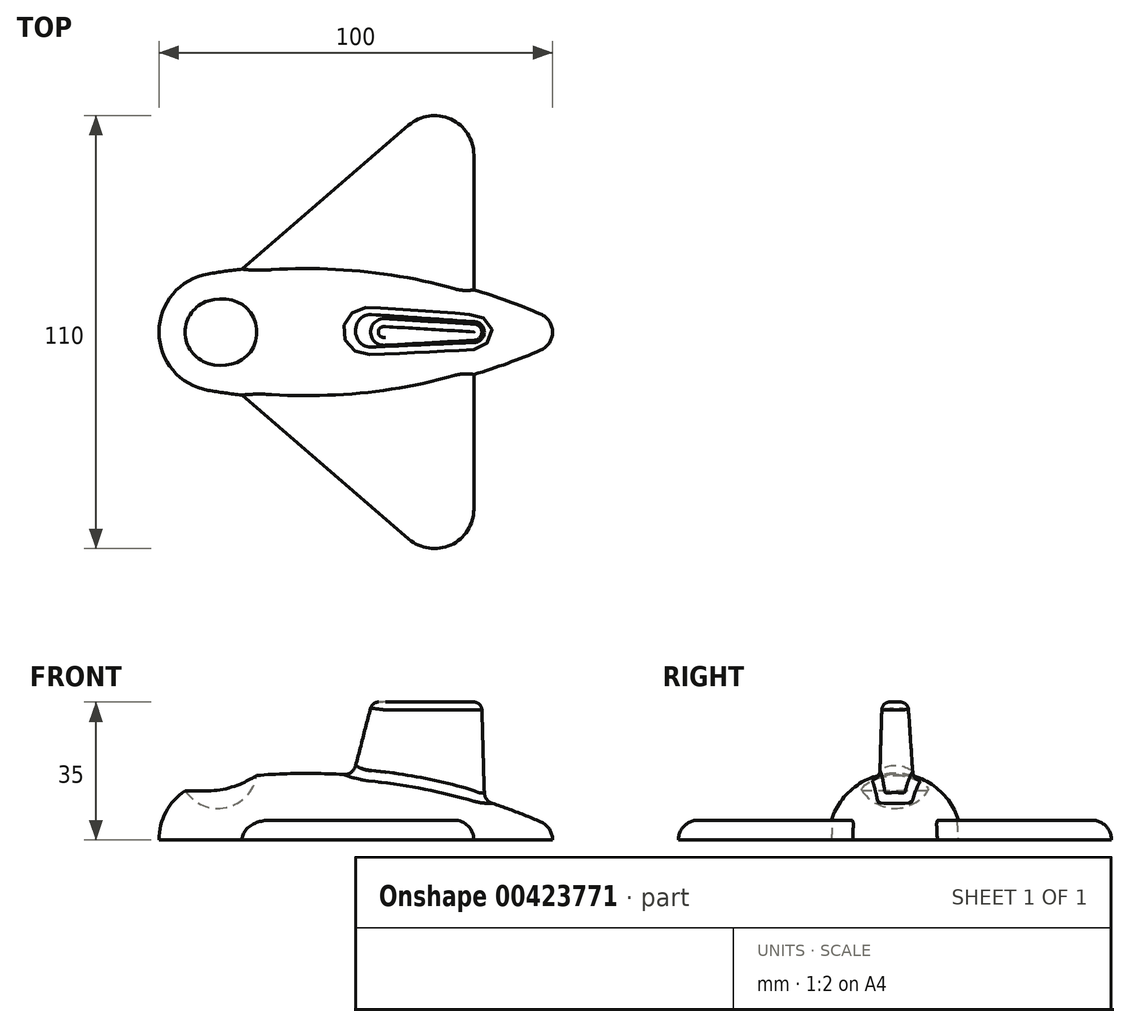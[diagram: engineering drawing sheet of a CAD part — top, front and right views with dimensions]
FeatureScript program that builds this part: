
annotation { "Feature Type Name" : "Feature", "Feature Type Description" : "" }
export const myFeature = defineFeature(function(context is Context, id is Id, definition is map)
    precondition{}
    {
        {
            var Q0;
            Q0=qCreatedBy(makeId("Top.planeOp"),FACE);
            var sketch = newSketch(context, id + "F0", { "sketchPlane" : qUnion([Q0])});
            skArc(sketch, "E0", {"start": v(-60.05, 14.8) * mm, "mid": v(-69, 9.68) * mm, "end": v(-72.55, 0) * mm});
            skArc(sketch, "E1", {"start": v(27.45, 0) * mm, "mid": v(26.63, 2.75) * mm, "end": v(24.44, 4.6) * mm});
            skArc(sketch, "E2", {"start": v(24.44, 4.6) * mm, "mid": v(-17.07, 15.8) * mm, "end": v(-60.05, 14.8) * mm});
            skLineSegment(sketch, "E3", {"start": v(-72.55, 0) * mm, "end": v(27.45, 0) * mm});
            skPoint(sketch, "E4.orphan", {"position": v(-79.31, 0) * mm});
            skSolve(sketch);
        }
        {
            var Q0;
            Q0=makeQuery(id+"F0.imprint","IMPRINT",FACE,{"disambiguationData":[TD([[makeQuery(id+"F0.imprint","IMPRINT",EDGE,{"derivedFrom":sQuery(id+"F0.wireOp",EDGE,"E0")}),1.0]])]});
            var Q1;
            Q1=sQuery(id+"F0.wireOp",EDGE,"E3");
            revolve(context, id + "F1", {"entities" : qUnion([Q0]), "axis" : qUnion([Q1]), "revolveType" : RevolveType.ONE_DIRECTION, "angle" : 180 * degree});
        }
        {
            var Q0;
            Q0=qCreatedBy(makeId("Front.planeOp"),FACE);
            var sketch = newSketch(context, id + "F2", { "sketchPlane" : qUnion([Q0])});
            skArc(sketch, "E5", {"start": v(-67.55, 18) * mm, "mid": v(-57.55, 8) * mm, "end": v(-47.55, 18) * mm});
            skLineSegment(sketch, "E6", {"start": v(-67.55, 18) * mm, "end": v(-47.55, 18) * mm});
            skPoint(sketch, "E7.orphan", {"position": v(-75.97, 18) * mm});
            skPoint(sketch, "E8.0.0.end.orphan", {"position": v(-72.55, 0) * mm});
            skPoint(sketch, "E8.0.0.start.orphan", {"position": v(-60.05, 0) * mm});
            skSolve(sketch);
        }
        {
            var Q0;
            Q0=makeQuery(id+"F2.imprint","IMPRINT",FACE,{"disambiguationData":[TD([[makeQuery(id+"F2.imprint","IMPRINT",EDGE,{"derivedFrom":sQuery(id+"F2.wireOp",EDGE,"E5")}),1.0]])]});
            var Q1;
            Q1=sQuery(id+"F2.wireOp",EDGE,"E6");
            revolve(context, id + "F3", {"operationType" : NewBodyOperationType.REMOVE, "entities" : qUnion([Q0]), "axis" : qUnion([Q1]), "revolveType" : RevolveType.FULL, "oppositeDirection" : true});
        }
        {
            var Q0;
            Q0=qCreatedBy(makeId("Top.planeOp"),FACE);
            var sketch = newSketch(context, id + "F4", { "sketchPlane" : qUnion([Q0])});
            skArc(sketch, "E9", {"start": v(7.45, 45) * mm, "mid": v(1.61, 54.1) * mm, "end": v(-9.08, 52.57) * mm});
            skLineSegment(sketch, "E10", {"start": v(-9.08, 52.57) * mm, "end": v(-51.58, 15.86) * mm});
            skLineSegment(sketch, "E11", {"start": v(7.45, 45) * mm, "end": v(7.45, 10.74) * mm});
            skLineSegment(sketch, "E12", {"start": v(7.45, 10.74) * mm, "end": v(7.45, 3.64) * mm});
            skLineSegment(sketch, "E13", {"start": v(7.45, 3.64) * mm, "end": v(-51.58, 11.7) * mm});
            skLineSegment(sketch, "E14", {"start": v(-51.58, 15.86) * mm, "end": v(-52.92, 14.7) * mm});
            skLineSegment(sketch, "E15", {"start": v(-52.92, 14.7) * mm, "end": v(-51.58, 11.7) * mm});
            skSolve(sketch);
        }
        {
            var Q0;
            Q0=makeQuery(id+"F4.imprint","IMPRINT",FACE,{"disambiguationData":[TD([[makeQuery(id+"F4.imprint","IMPRINT",EDGE,{"derivedFrom":sQuery(id+"F4.wireOp",EDGE,"E9")}),1.0]])]});
            extrude(context, id + "F5", {"entities" : qUnion([Q0]), "operationType" : NewBodyOperationType.ADD, "depth" : 5 * mm});
        }
        {
            var Q0;
            Q0=makeQuery(id+"F1.opRevolve","SWEPT_BODY",BODY,{"disambiguationData":[OSD([sQuery(id+"F0.wireOp",EDGE,"E0"),sQuery(id+"F0.wireOp",EDGE,"E1"),sQuery(id+"F0.wireOp",EDGE,"E2"),sQuery(id+"F0.wireOp",EDGE,"E3")])]});
            var Q1;
            Q1=qCreatedBy(makeId("Front.planeOp"),FACE);
            mirror(context, id + "F6", {"operationType" : NewBodyOperationType.ADD, "entities" : qUnion([Q0]), "mirrorPlane" : qUnion([Q1])});
        }
        {
            var Q0;
            Q0=makeQuery(id+"F6.opPattern","COPY",EDGE,{"derivedFrom":makeQuery(id+"F5.opExtrude","CAP_EDGE",EDGE,{"disambiguationData":[OSD([sQuery(id+"F4.wireOp",EDGE,"E10"),sQuery(id+"F4.wireOp",EDGE,"E14")])],"isStart":false}),"instanceName":"1"});
            var Q1;
            Q1=makeQuery(id+"F5.opExtrude","CAP_EDGE",EDGE,{"disambiguationData":[OSD([sQuery(id+"F4.wireOp",EDGE,"E10"),sQuery(id+"F4.wireOp",EDGE,"E14")])],"isStart":false});
            fillet(context, id + "F7", {"entities" : qUnion([Q0, Q1]), "radius" : 5 * mm, "tangentPropagation" : true, "allowEdgeOverflow" : false});
        }
        {
            var Q0;
            Q0=qCreatedBy(makeId("Top.planeOp"),FACE);
            cPlane(context, id + "F8", {"entities" : qUnion([Q0]), "cplaneType" : CPlaneType.OFFSET, "offset" : 35 * mm, "width" : 150 * mm, "height" : 150 * mm});
        }
        {
            var Q0;
            Q0=qCreatedBy(id+"F8.planeOp",FACE);
            var sketch = newSketch(context, id + "F9", { "sketchPlane" : qUnion([Q0])});
            skArc(sketch, "E16", {"start": v(7.57, -2) * mm, "mid": v(9.45, 0) * mm, "end": v(7.57, 2) * mm});
            skArc(sketch, "E17", {"start": v(-14.86, 3.3) * mm, "mid": v(-18.35, 0) * mm, "end": v(-14.86, -3.3) * mm});
            skLineSegment(sketch, "E18", {"start": v(-14.86, 3.3) * mm, "end": v(7.57, 2) * mm});
            skLineSegment(sketch, "E19", {"start": v(-14.86, -3.3) * mm, "end": v(7.57, -2) * mm});
            skSolve(sketch);
        }
        {
            var Q0;
            Q0=qCreatedBy(makeId("Top.planeOp"),FACE);
            var sketch = newSketch(context, id + "F10", { "sketchPlane" : qUnion([Q0])});
            skPoint(sketch, "E20.0", {"position": v(7.45, 0) * mm});
            skArc(sketch, "E21", {"start": v(-22.1, 5.65) * mm, "mid": v(-27.55, 0.78) * mm, "end": v(-22.33, -4.33) * mm});
            skArc(sketch, "E22", {"start": v(7.59, -3) * mm, "mid": v(10.45, -0.07) * mm, "end": v(7.72, 2.99) * mm});
            skLineSegment(sketch, "E23", {"start": v(-22.1, 5.65) * mm, "end": v(7.72, 2.99) * mm});
            skLineSegment(sketch, "E24", {"start": v(-22.33, -4.33) * mm, "end": v(7.59, -3) * mm});
            skSolve(sketch);
        }
        {
            var Q0;
            Q0=makeQuery(id+"F9.imprint","IMPRINT",FACE,{"disambiguationData":[TD([[makeQuery(id+"F9.imprint","IMPRINT",EDGE,{"derivedFrom":sQuery(id+"F9.wireOp",EDGE,"E16")}),1.0]])]});
            var Q1;
            Q1=makeQuery(id+"F10.imprint","IMPRINT",FACE,{"disambiguationData":[TD([[makeQuery(id+"F10.imprint","IMPRINT",EDGE,{"derivedFrom":sQuery(id+"F10.wireOp",EDGE,"E21")}),1.0]])]});
            loft(context, id + "F11", {"sheetProfilesArray" : [{ "sheetProfileEntities" : qUnion([Q0]) }, { "sheetProfileEntities" : qUnion([Q1]) }]});
        }
        {
            var Q0;
            Q0=makeQuery(id+"F11.opLoft","MID_CAP_EDGE",EDGE,{"disambiguationData":[OSD([sQuery(id+"F9.wireOp",EDGE,"E16"),sQuery(id+"F9.wireOp",EDGE,"E17"),sQuery(id+"F9.wireOp",EDGE,"E19")])],"capPos":0.0});
            fillet(context, id + "F12", {"entities" : qUnion([Q0]), "radius" : 2 * mm, "tangentPropagation" : true, "allowEdgeOverflow" : false});
        }
        {
            var Q0;
            Q0=makeQuery(id+"F1.opRevolve","SWEPT_BODY",BODY,{"disambiguationData":[OSD([sQuery(id+"F0.wireOp",EDGE,"E0"),sQuery(id+"F0.wireOp",EDGE,"E1"),sQuery(id+"F0.wireOp",EDGE,"E2"),sQuery(id+"F0.wireOp",EDGE,"E3")])]});
            var Q1;
            Q1=makeQuery(id+"F11.opLoft","SWEPT_BODY",BODY,{"disambiguationData":[OSD([makeQuery(id+"F9.imprint","IMPRINT",FACE,{"disambiguationData":[TD([[makeQuery(id+"F9.imprint","IMPRINT",EDGE,{"derivedFrom":sQuery(id+"F9.wireOp",EDGE,"E16")}),1.0]])]}),makeQuery(id+"F10.imprint","IMPRINT",FACE,{"disambiguationData":[TD([[makeQuery(id+"F10.imprint","IMPRINT",EDGE,{"derivedFrom":sQuery(id+"F10.wireOp",EDGE,"E21")}),1.0]])]})])]});
            booleanBodies(context, id + "F13", {"operationType" : BooleanOperationType.UNION, "tools" : qUnion([Q0, Q1])});
        }
        {
            var Q0;
            Q0=makeQuery(id+"F13.opBoolean","INTERSECT",EDGE,{"derivedFrom":[makeQuery(id+"F1.opRevolve","SWEPT_FACE",FACE,{"disambiguationData":[OSD([sQuery(id+"F0.wireOp",EDGE,"E2")])]}),makeQuery(id+"F11.opLoft","SWEPT_FACE",FACE,{"disambiguationData":[OSD([sQuery(id+"F9.wireOp",EDGE,"E16"),sQuery(id+"F9.wireOp",EDGE,"E17"),sQuery(id+"F9.wireOp",EDGE,"E19"),sQuery(id+"F10.wireOp",EDGE,"E21"),sQuery(id+"F10.wireOp",EDGE,"E22"),sQuery(id+"F10.wireOp",EDGE,"E24")])]})]});
            fillet(context, id + "F14", {"entities" : qUnion([Q0]), "radius" : 3 * mm, "tangentPropagation" : true, "allowEdgeOverflow" : false});
        }
    });
